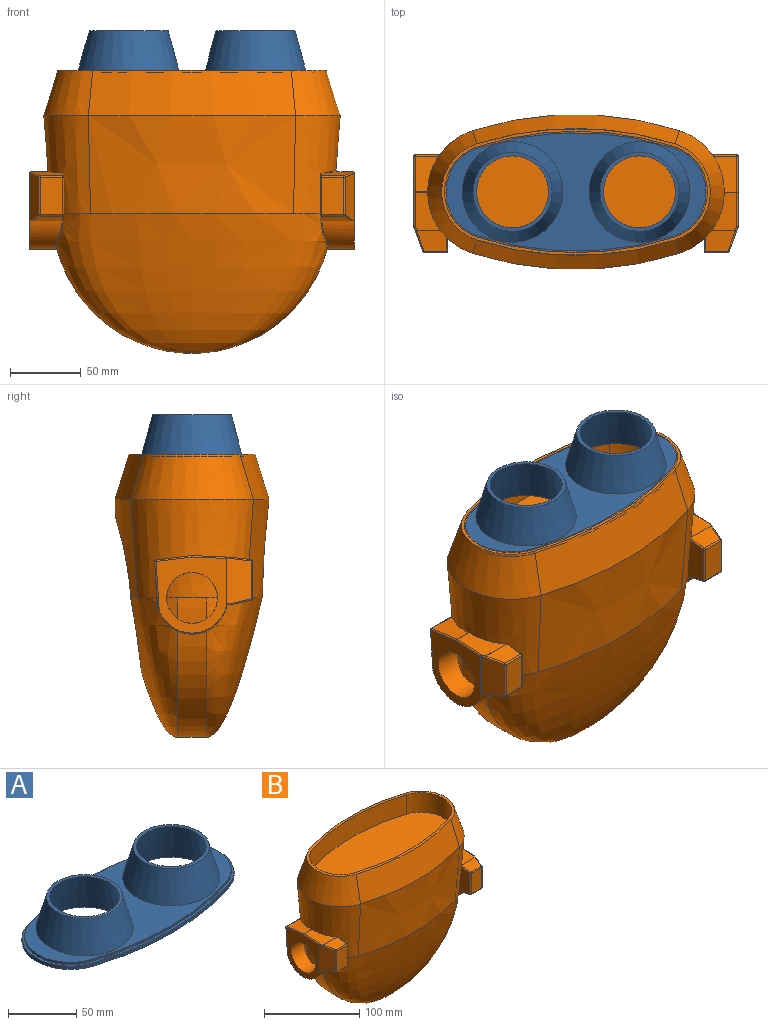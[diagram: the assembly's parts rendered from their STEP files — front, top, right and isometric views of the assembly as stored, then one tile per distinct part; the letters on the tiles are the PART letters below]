
ASSEMBLY  parts=2 mates=1
PART A: 17 faces, bbox 190.4x90.1x33 mm
  f0: cylinder r=230.24mm len=140.85mm, axis (0,0,-1), area 429.4mm2, adj f1,f3,f4,f5
  f1: cylinder r=35.71mm len=68mm, axis (0,0,-1), area 270mm2, adj f0,f2,f4,f5
  f2: cylinder r=230.24mm len=140.85mm, axis (0,0,-1), area 429.4mm2, adj f1,f3,f4,f5
  f3: cylinder r=35.71mm len=68mm, axis (0,0,-1), area 270mm2, adj f0,f2,f4,f5
  f4: plane 190.42x90.07mm, normal (0,0,1), area 919.9mm2, adj f0,f1,f2,f3,f6,f7,f8,f9
  f5: plane 190.42x90.07mm, normal (0,0,-1), area 7227.7mm2, adj f0,f1,f2,f3,f15,f16
  f6: cylinder r=33.71mm len=64.19mm, axis (0,0,-1), area 169.9mm2, adj f4,f7,f9,f10
  f7: cylinder r=228.24mm len=139.62mm, axis (0,0,-1), area 283.8mm2, adj f4,f6,f8,f10
  f8: cylinder r=33.71mm len=64.19mm, axis (0,0,-1), area 169.9mm2, adj f4,f7,f9,f10
  f9: cylinder r=228.24mm len=139.62mm, axis (0,0,-1), area 283.8mm2, adj f4,f6,f8,f10
  f10: plane 186.42x86.07mm, normal (0,0,1), area 5227.2mm2, adj f6,f7,f8,f9,f12,f14
  f11: plane 56x56mm, normal (0,0,1), area 420.2mm2, adj f12,f15
  f12: cone r=35.65mm half-angle=15.3deg, axis (0,0,-1), area 5803.6mm2, adj f10,f11
  f13: plane 56x56mm, normal (0,0,1), area 420.2mm2, adj f14,f16
  f14: cone r=35.65mm half-angle=15.3deg, axis (0,0,-1), area 5803.6mm2, adj f10,f13
  f15: cone r=25.5mm half-angle=13deg, axis (0,0,-1), area 6241mm2, adj f5,f11
  f16: cone r=33.15mm half-angle=13deg, axis (0,0,-1), area 6241mm2, adj f5,f13
PART B: 117 faces, bbox 230.5x110.5x201.4 mm
  f0: cylinder r=55mm len=9.8mm, axis (0,-0.98,0.17), area 0mm2, adj f3,f116
  f1: cylinder r=55mm len=9.8mm, axis (0,-0.98,0.17), area 0mm2, adj f3,f116
  f2: bspline ~197.93x98.96mm, area 13482.6mm2, adj f3,f4,f5,f12,f76,f78,f80,f109
  f3: cone r=240.24mm half-angle=4.1deg, axis (0,0,1), area 5406.7mm2, adj f0,f1,f2,f4,f8,f12,f114,f115
  f4: cone r=45.71mm half-angle=4.1deg, axis (0,0,1), area 5975.1mm2, adj f2,f3,f6,f11,f13,f19,f24,f25
  f5: cylinder r=98.96mm len=192.14mm, axis (0,1,0), area 5203.4mm2, adj f2,f6,f76,f109
  f6: bspline ~197.93x98.96mm, area 18107.9mm2, adj f4,f5,f12,f13,f22,f28,f35,f44
  f7: plane 190.42x90.07mm, normal (0,0,1), area 1370.5mm2, adj f8,f9,f10,f11,f14,f15,f16,f17
  f8: cone r=230.24mm half-angle=17.4deg, axis (0,0,-1), area 4903.1mm2, adj f3,f7,f9,f11
  f9: cone r=35.71mm half-angle=17.4deg, axis (0,0,-1), area 3439.4mm2, adj f7,f8,f10,f12
  f10: cone r=230.24mm half-angle=17.4deg, axis (0,0,-1), area 4903.1mm2, adj f7,f9,f11,f13
  f11: cone r=35.71mm half-angle=17.4deg, axis (0,0,-1), area 3439.4mm2, adj f4,f7,f8,f10
  f12: cone r=45.71mm half-angle=4.1deg, axis (0,0,1), area 5910.8mm2, adj f2,f3,f6,f9,f13,f40,f44,f55
  f13: cone r=240.24mm half-angle=4.1deg, axis (0,0,1), area 10372.5mm2, adj f4,f6,f10,f12
  f14: cylinder r=227.24mm len=139.01mm, axis (0,0,1), area 3531.9mm2, adj f7,f15,f17,f18
  f15: cylinder r=32.71mm len=62.29mm, axis (0,0,1), area 2060.7mm2, adj f7,f14,f16,f18
  f16: cylinder r=227.24mm len=139.01mm, axis (0,0,1), area 3531.9mm2, adj f7,f15,f17,f18
  f17: cylinder r=32.71mm len=62.29mm, axis (0,0,1), area 2060.7mm2, adj f7,f14,f16,f18
  f18: plane 184.42x84.07mm, normal (0,0,1), area 12760.2mm2, adj f14,f15,f16,f17
  f19: plane 20.89x14.27mm, normal (0,-0.12,0.99), area 262.8mm2, adj f4,f81,f86,f93,f94
  f20: plane 26.68x15.7mm, normal (0,-1,0), area 418.9mm2, adj f82,f84,f86,f87
  f21: plane 20.91x14.3mm, normal (0,-0.24,-0.97), area 269.4mm2, adj f84,f89,f91,f92
  f22: plane 22.85x2.9mm, normal (0,0,-1), area 63.9mm2, adj f6,f23,f89,f92,f97,f107
  f23: cylinder r=25mm len=49.15mm, axis (-1,0,0), area 1345mm2, adj f22,f29,f97,f99,f107,f108,f109,f110
  f24: plane 30.73x21.86mm, normal (0,1,-0.06), area 665.7mm2, adj f4,f104,f108,f110,f113
  f25: plane 25.51x20.41mm, normal (0,0.12,0.99), area 372.3mm2, adj f4,f101,f104,f105
  f26: cylinder r=18mm len=36mm, axis (-1,0,0), area 2076.7mm2, adj f29,f31,f32,f33,f34
  f27: plane 27.47x21.8mm, normal (0,-0.04,1), area 405.5mm2, adj f4,f93,f98,f101,f102
  f28: plane 32.25x16.41mm, normal (1,0,0), area 428mm2, adj f4,f6,f81,f82,f89
  f29: plane 54x49.86mm, normal (-1,0,0), area 1324.9mm2, adj f23,f26,f99,f102,f105,f108
  f30: plane 20x1.25mm, normal (0,0,-1), area 16.7mm2, adj f33,f34
  f31: bspline ~14.97x8mm, area 62.1mm2, adj f26,f33,f34
  f32: bspline ~25.66x12.57mm, area 62.1mm2, adj f26,f33,f34
  f33: cylinder r=98.96mm len=20mm, axis (0,1,0), area 342.2mm2, adj f26,f30,f31,f32
  f34: cone r=45.71mm half-angle=4.1deg, axis (0,0,1), area 523.5mm2, adj f26,f30,f31,f32
  f35: plane 23.89x3.02mm, normal (0,0,-1), area 69mm2, adj f6,f36,f43,f45,f53,f63,f65,f73
  f36: cylinder r=25mm len=48.99mm, axis (1,0,0), area 1345.6mm2, adj f35,f37,f45,f69,f73,f76,f78
  f37: plane 30.8x21.86mm, normal (0,1,-0.06), area 657.5mm2, adj f36,f69,f74,f78,f79,f80
  f38: plane 25.59x19.17mm, normal (0,0.12,0.99), area 344.7mm2, adj f39,f70,f72,f74,f75
  f39: plane 27.51x20.39mm, normal (0,-0.04,1), area 375.8mm2, adj f38,f40,f66,f68,f72
  f40: plane 28.52x21.05mm, normal (0,-0.12,0.99), area 268.2mm2, adj f12,f39,f55,f60,f64,f66,f72
  f41: plane 26.68x15.75mm, normal (0,-1,0), area 420.2mm2, adj f54,f58,f59,f60
  f42: cylinder r=18mm len=36mm, axis (1,0,0), area 2076.7mm2, adj f45,f47,f48,f49,f50
  f43: plane 21x14.42mm, normal (0,-0.24,-0.97), area 272.6mm2, adj f35,f53,f58,f63
  f44: plane 32.25x16.41mm, normal (-1,0,0), area 428mm2, adj f6,f12,f53,f54,f55
  f45: plane 54x49.99mm, normal (1,0,0), area 1329.3mm2, adj f35,f36,f42,f65,f68,f69,f70
  f46: plane 20x1.25mm, normal (0,0,-1), area 16.7mm2, adj f47,f50
  f47: cone r=45.71mm half-angle=4.1deg, axis (0,0,1), area 523.4mm2, adj f42,f46,f48,f49
  f48: bspline ~25.66x12.57mm, area 62.1mm2, adj f42,f47,f50
  f49: bspline ~14.97x8mm, area 62.1mm2, adj f42,f47,f50
  f50: cylinder r=98.96mm len=20mm, axis (0,1,0), area 342.2mm2, adj f42,f46,f48,f49
  f51: plane 31.96x17.31mm, normal (-0.94,-0.34,0), area 547.4mm2, adj f87,f91,f94,f97,f98,f99
  f52: plane 32.65x17.18mm, normal (0.94,-0.34,0), area 543.9mm2, adj f59,f63,f64,f65,f66
  f53: cylinder r=1mm len=16.86mm, axis (0,-0.97,0.24), area 25.2mm2, adj f6,f35,f43,f44,f56
  f54: cylinder r=1mm len=26.68mm, axis (0,0,1), area 41.9mm2, adj f41,f44,f56,f57
  f55: cylinder r=1mm len=14.13mm, axis (0,0.99,0.12), area 21.3mm2, adj f12,f40,f44,f57
  f56: sphere r=1mm, area 0.9mm2, adj f53,f54,f58
  f57: sphere r=1mm, area 1mm2, adj f54,f55,f60
  f58: cylinder r=1mm len=15.75mm, axis (1,0,0), area 21mm2, adj f41,f43,f56,f61
  f59: cylinder r=1mm len=26.68mm, axis (0,0,-1), area 32.6mm2, adj f41,f52,f61,f62
  f60: cylinder r=1mm len=15.75mm, axis (1,0,0), area 22.9mm2, adj f40,f41,f57,f62
  f61: sphere r=1mm, area 0.7mm2, adj f58,f59,f63
  f62: sphere r=1mm, area 0.7mm2, adj f59,f60,f64
  f63: cylinder r=1mm len=17.62mm, axis (0.33,0.92,-0.22), area 25.8mm2, adj f35,f43,f52,f61,f65
  f64: cylinder r=1mm len=14.54mm, axis (-0.34,-0.93,-0.11), area 23.4mm2, adj f40,f52,f62,f66
  f65: cylinder r=1mm len=32.95mm, axis (0,0,1), area 11.5mm2, adj f35,f45,f52,f63,f67
  f66: cylinder r=1mm len=3.25mm, axis (-0.34,-0.94,-0.04), area 4.9mm2, adj f39,f40,f52,f64,f67
  f67: sphere r=1mm, area 0.3mm2, adj f65,f66,f68
  f68: cylinder r=1mm len=24.6mm, axis (0,-1,-0.04), area 38.6mm2, adj f39,f45,f67,f70
  f69: cylinder r=1mm len=35.19mm, axis (0,0.06,1), area 51.9mm2, adj f36,f37,f45,f71
  f70: cylinder r=1mm len=25.72mm, axis (0,-0.99,0.12), area 40.4mm2, adj f38,f45,f68,f71
  f71: sphere r=1mm, area 1mm2, adj f69,f70,f74
  f72: bspline ~27.61x10.61mm, area 38.7mm2, adj f12,f38,f39,f40,f75
  f73: bspline ~20.22x16.34mm, area 26.3mm2, adj f6,f35,f36,f76
  f74: cylinder r=1mm len=20.7mm, axis (1,0,0), area 30.1mm2, adj f37,f38,f71,f77
  f75: bspline ~25.68x9.4mm, area 43.7mm2, adj f12,f38,f72,f77
  f76: bspline ~22.43x3.24mm, area 26.7mm2, adj f2,f5,f6,f36,f73,f78
  f77: bspline ~2.71x2.43mm, area 3.1mm2, adj f12,f74,f75,f79
  f78: bspline ~20.89x15.87mm, area 26.2mm2, adj f2,f36,f37,f76,f80
  f79: bspline ~50.01x3.57mm, area 23.1mm2, adj f12,f37,f77,f80
  f80: bspline ~19.01x1.62mm, area 4.5mm2, adj f2,f37,f78,f79
  f81: cylinder r=1mm len=14.13mm, axis (0,0.99,0.12), area 21.3mm2, adj f4,f19,f28,f83
  f82: cylinder r=1mm len=26.68mm, axis (0,0,1), area 41.9mm2, adj f20,f28,f83,f85
  f83: sphere r=1mm, area 1mm2, adj f81,f82,f86
  f84: cylinder r=1mm len=15.7mm, axis (-1,0,0), area 20.9mm2, adj f20,f21,f85,f88
  f85: sphere r=1mm, area 1.4mm2, adj f82,f84,f89
  f86: cylinder r=1mm len=15.7mm, axis (-1,0,0), area 22.8mm2, adj f19,f20,f83,f90
  f87: cylinder r=1mm len=26.68mm, axis (0,0,-1), area 32.6mm2, adj f20,f51,f88,f90
  f88: sphere r=1mm, area 0.7mm2, adj f84,f87,f91
  f89: cylinder r=1mm len=16.86mm, axis (0,-0.97,0.24), area 25.2mm2, adj f6,f21,f22,f28,f85,f92
  f90: sphere r=1mm, area 0.7mm2, adj f86,f87,f94
  f91: cylinder r=1mm len=14.47mm, axis (-0.33,0.92,-0.22), area 23.3mm2, adj f21,f51,f88,f95
  f92: cylinder r=1mm len=21.14mm, axis (-1,0,0), area 5mm2, adj f21,f22,f89,f95
  f93: cylinder r=1mm len=20.67mm, axis (-1,0,0), area 1.5mm2, adj f4,f19,f27,f96
  f94: cylinder r=1mm len=14.51mm, axis (0.34,-0.93,-0.11), area 23.4mm2, adj f19,f51,f90,f96
  f95: sphere r=1mm, area 0.2mm2, adj f91,f92,f97
  f96: sphere r=1mm, area 0.1mm2, adj f93,f94,f98
  f97: cylinder r=1mm len=3.44mm, axis (-0.34,0.94,0), area 5.1mm2, adj f22,f23,f51,f95,f99
  f98: cylinder r=1mm len=3.35mm, axis (0.34,-0.94,-0.04), area 5mm2, adj f27,f51,f96,f100
  f99: cylinder r=1mm len=33.47mm, axis (0,0,1), area 11.4mm2, adj f23,f29,f51,f97,f100
  f100: sphere r=1mm, area 0.3mm2, adj f98,f99,f102
  f101: cylinder r=1mm len=11.65mm, axis (-1,0,0), area 1.9mm2, adj f4,f25,f27,f103
  f102: cylinder r=1mm len=24.39mm, axis (0,-1,-0.04), area 38.3mm2, adj f27,f29,f100,f103
  f103: sphere r=1mm, area 0.2mm2, adj f101,f102,f105
  f104: cylinder r=1mm len=21.18mm, axis (-1,0,0), area 31.4mm2, adj f4,f24,f25,f106
  f105: cylinder r=1mm len=25.63mm, axis (0,-0.99,0.12), area 40.4mm2, adj f25,f29,f103,f106
  f106: sphere r=1mm, area 1mm2, adj f104,f105,f108
  f107: bspline ~20.22x16.34mm, area 26.3mm2, adj f6,f22,f23,f109
  f108: cylinder r=1mm len=35.19mm, axis (0,0.06,1), area 51.3mm2, adj f23,f24,f29,f106,f110
  f109: bspline ~22.62x3.39mm, area 26.7mm2, adj f2,f5,f6,f23,f107,f111
  f110: cylinder r=1mm len=21.99mm, axis (-1,0,0), area 3.1mm2, adj f23,f24,f108,f112
  f111: bspline ~20.89x15.87mm, area 26.1mm2, adj f2,f23,f109,f112
  f112: bspline ~0.81x0.79mm, area 0.2mm2, adj f2,f110,f111,f113
  f113: bspline ~30.58x2.38mm, area 9.6mm2, adj f2,f4,f24,f112
  f114: cylinder r=55mm len=94.01mm, axis (0,0.98,-0.17), area 0mm2, adj f3,f116
  f115: cylinder r=55mm len=110mm, axis (0,0.98,-0.17), area 259.8mm2, adj f2,f3,f116
  f116: plane 110.44x108.77mm, normal (0,0.98,-0.17), area 9503.3mm2, adj f0,f1,f114,f115
PLACE A t=(25.37,-39.08,14.88)mm
PLACE B t=(25.37,-39.08,19.88)mm fixed
MATE fastened B.f7 <-> A.f10  axis (0,0,1) through (25.37,-39.08,19.88)mm
